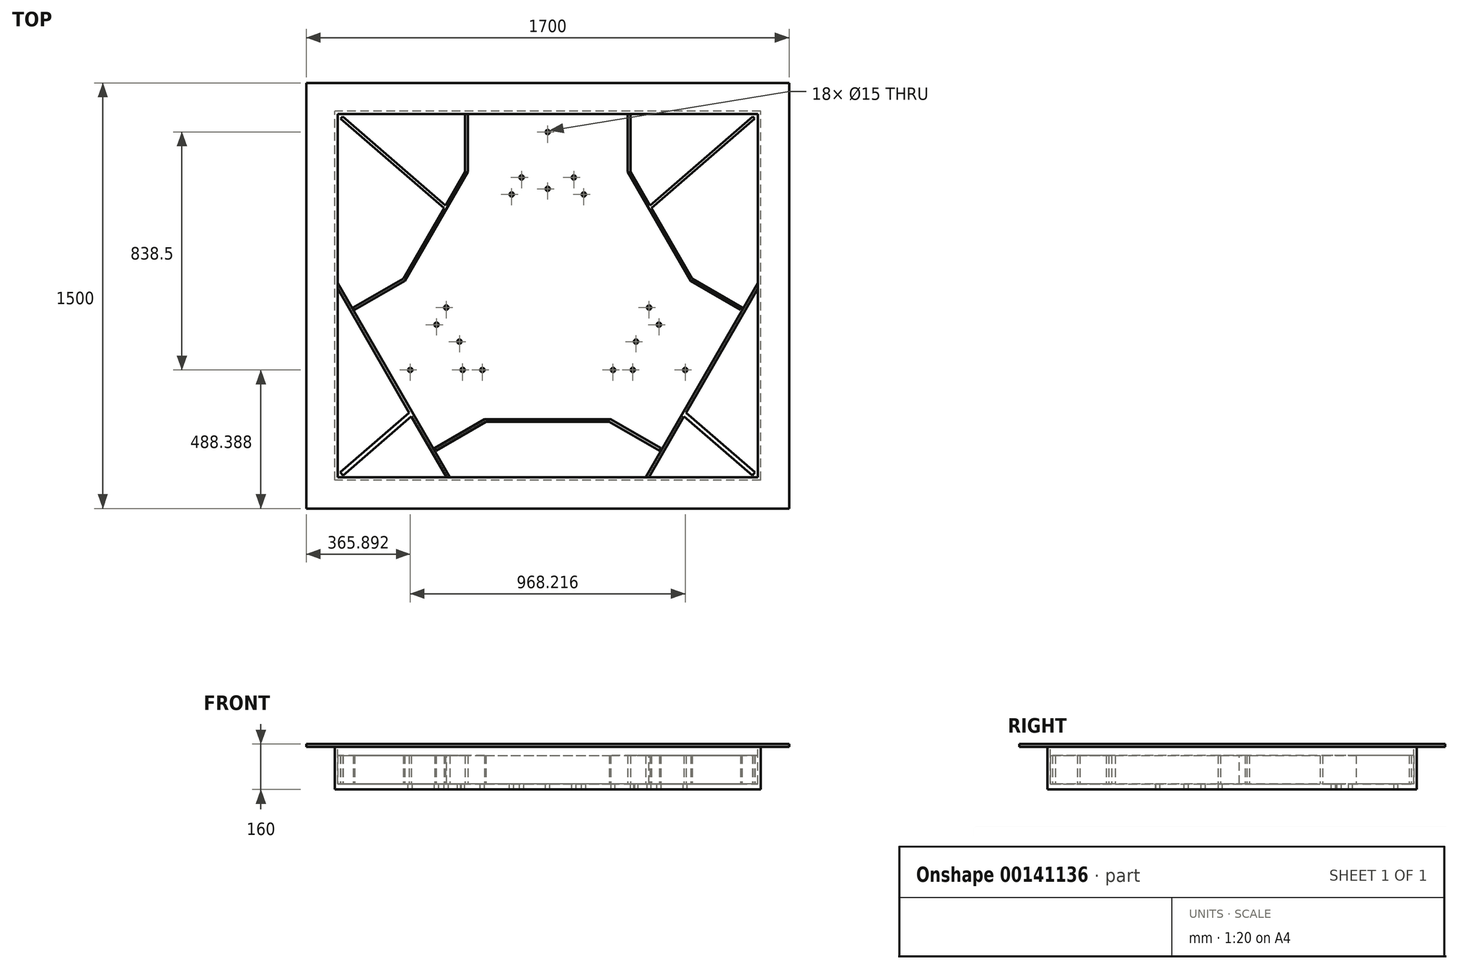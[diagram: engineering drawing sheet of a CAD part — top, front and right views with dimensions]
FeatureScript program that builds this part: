
annotation { "Feature Type Name" : "Feature", "Feature Type Description" : "" }
export const myFeature = defineFeature(function(context is Context, id is Id, definition is map)
    precondition{}
    {
        {
            var Q0;
            Q0=qCreatedBy(makeId("Top.planeOp"),FACE);
            var sketch = newSketch(context, id + "F0", { "sketchPlane" : qUnion([Q0])});
            skLineSegment(sketch, "E0.bottom", {"start": v(750, -650) * mm, "end": v(-750, -650) * mm});
            skLineSegment(sketch, "E0.top", {"start": v(750, 650) * mm, "end": v(-750, 650) * mm});
            skLineSegment(sketch, "E0.left", {"start": v(750, -650) * mm, "end": v(750, 650) * mm});
            skLineSegment(sketch, "E0.right", {"start": v(-750, -650) * mm, "end": v(-750, 650) * mm});
            skPoint(sketch, "E0.middle", {"position": v(0, 0) * mm});
            skSolve(sketch);
        }
        {
            var Q0;
            Q0 = qSketchRegion(id + "F0", true);
            extrude(context, id + "F1", {"entities" : qUnion([Q0]), "depth" : 150 * mm});
        }
        {
            var Q0;
            Q0=makeQuery(id+"F1.opExtrude","CAP_FACE",FACE,{"disambiguationData":[OSD([sQuery(id+"F0.wireOp",EDGE,"E0.bottom"),sQuery(id+"F0.wireOp",EDGE,"E0.top"),sQuery(id+"F0.wireOp",EDGE,"E0.left"),sQuery(id+"F0.wireOp",EDGE,"E0.right")])],"isStart":false});
            var sketch = newSketch(context, id + "F2", { "sketchPlane" : qUnion([Q0])});
            skLineSegment(sketch, "E1", {"start": v(-750, 0) * mm, "end": v(750, 0) * mm, "construction": true});
            skLineSegment(sketch, "E2.bottom", {"start": v(740, -640) * mm, "end": v(-740, -640) * mm});
            skLineSegment(sketch, "E2.top", {"start": v(740, 640) * mm, "end": v(-740, 640) * mm});
            skLineSegment(sketch, "E2.left", {"start": v(740, -640) * mm, "end": v(740, 640) * mm});
            skLineSegment(sketch, "E2.right", {"start": v(-740, -640) * mm, "end": v(-740, 640) * mm});
            skPoint(sketch, "E2.middle", {"position": v(0, 0) * mm});
            skSolve(sketch);
        }
        {
            var Q0;
            Q0 = qSketchRegion(id + "F2", true);
            extrude(context, id + "F3", {"entities" : qUnion([Q0]), "operationType" : NewBodyOperationType.REMOVE, "oppositeDirection" : true, "depth" : 130 * mm});
        }
        {
            var Q0;
            Q0=makeQuery(id+"F1.opExtrude","CAP_FACE",FACE,{"disambiguationData":[OSD([sQuery(id+"F0.wireOp",EDGE,"E0.bottom"),sQuery(id+"F0.wireOp",EDGE,"E0.top"),sQuery(id+"F0.wireOp",EDGE,"E0.left"),sQuery(id+"F0.wireOp",EDGE,"E0.right")])],"isStart":false});
            var sketch = newSketch(context, id + "F4", { "sketchPlane" : qUnion([Q0])});
            skLineSegment(sketch, "E3", {"start": v(0, 650) * mm, "end": v(0, -650) * mm, "construction": true});
            skLineSegment(sketch, "E4.bottom", {"start": v(850, -750) * mm, "end": v(-850, -750) * mm});
            skLineSegment(sketch, "E4.top", {"start": v(850, 750) * mm, "end": v(-850, 750) * mm});
            skLineSegment(sketch, "E4.left", {"start": v(850, -750) * mm, "end": v(850, 750) * mm});
            skLineSegment(sketch, "E4.right", {"start": v(-850, -750) * mm, "end": v(-850, 750) * mm});
            skPoint(sketch, "E4.middle", {"position": v(0, 0) * mm});
            skLineSegment(sketch, "E5.bottom", {"start": v(-740, 640) * mm, "end": v(740, 640) * mm});
            skLineSegment(sketch, "E5.top", {"start": v(-740, -640) * mm, "end": v(740, -640) * mm});
            skLineSegment(sketch, "E5.left", {"start": v(-740, 640) * mm, "end": v(-740, -640) * mm});
            skLineSegment(sketch, "E5.right", {"start": v(740, 640) * mm, "end": v(740, -640) * mm});
            skSolve(sketch);
        }
        {
            var Q0;
            Q0 = qSketchRegion(id + "F4", true);
            extrude(context, id + "F5", {"entities" : qUnion([Q0]), "operationType" : NewBodyOperationType.ADD, "depth" : 10 * mm});
        }
        {
            var Q0;
            Q0=makeQuery(id+"F3.boolean.opBoolean","COPY",FACE,{"derivedFrom":makeQuery(id+"F3.opExtrude","CAP_FACE",FACE,{"disambiguationData":[OSD([sQuery(id+"F2.wireOp",EDGE,"E2.bottom"),sQuery(id+"F2.wireOp",EDGE,"E2.top"),sQuery(id+"F2.wireOp",EDGE,"E2.left"),sQuery(id+"F2.wireOp",EDGE,"E2.right")])],"isStart":false})});
            var sketch = newSketch(context, id + "F6", { "sketchPlane" : qUnion([Q0])});
            skLineSegment(sketch, "E6", {"start": v(0, -640) * mm, "end": v(0, 640) * mm, "construction": true});
            skCircle(sketch, "E7", {"center": v(0, 17.89) * mm, "radius": 559 * mm, "construction": true});
            skCircle(sketch, "E8", {"center": v(0, 576.89) * mm, "radius": 7.5 * mm});
            skLineSegment(sketch, "E9", {"start": v(0, 17.89) * mm, "end": v(-275.24, -141.02) * mm, "construction": true});
            skLineSegment(sketch, "E10", {"start": v(0, 17.89) * mm, "end": v(329.13, -172.14) * mm, "construction": true});
            skCircle(sketch, "E11.MirrorC", {"center": v(-484.1, -261.61) * mm, "radius": 7.5 * mm});
            skCircle(sketch, "E12.MirrorC", {"center": v(484.1, -261.61) * mm, "radius": 7.5 * mm});
            skCircle(sketch, "E13", {"center": v(0, 17.89) * mm, "radius": 362 * mm, "construction": true});
            skCircle(sketch, "E14", {"center": v(0, 17.89) * mm, "radius": 409.5 * mm, "construction": true});
            skCircle(sketch, "E15", {"center": v(-92, 416.92) * mm, "radius": 7.5 * mm});
            skCircle(sketch, "E16.MirrorC", {"center": v(92, 416.92) * mm, "radius": 7.5 * mm});
            skCircle(sketch, "E17", {"center": v(-127, 356.88) * mm, "radius": 7.5 * mm});
            skCircle(sketch, "E18.MirrorC", {"center": v(127, 356.88) * mm, "radius": 7.5 * mm});
            skCircle(sketch, "E19.MirrorC", {"center": v(-230.07, -261.6) * mm, "radius": 7.5 * mm});
            skCircle(sketch, "E20.MirrorC", {"center": v(-357.07, -41.62) * mm, "radius": 7.5 * mm});
            skCircle(sketch, "E21.MirrorC", {"center": v(-299.57, -261.3) * mm, "radius": 7.5 * mm});
            skCircle(sketch, "E22.MirrorC", {"center": v(-391.57, -101.95) * mm, "radius": 7.5 * mm});
            skCircle(sketch, "E23.MirrorC", {"center": v(391.57, -101.95) * mm, "radius": 7.5 * mm});
            skCircle(sketch, "E24.MirrorC", {"center": v(299.57, -261.3) * mm, "radius": 7.5 * mm});
            skCircle(sketch, "E25.MirrorC", {"center": v(230.07, -261.6) * mm, "radius": 7.5 * mm});
            skCircle(sketch, "E26.MirrorC", {"center": v(357.07, -41.62) * mm, "radius": 7.5 * mm});
            skPoint(sketch, "E27.middle", {"position": v(0, 435.08) * mm});
            skCircle(sketch, "E28", {"center": v(0, 376.89) * mm, "radius": 7.5 * mm});
            skCircle(sketch, "E29.MirrorC", {"center": v(310.9, -161.61) * mm, "radius": 7.5 * mm});
            skCircle(sketch, "E30.MirrorC", {"center": v(-310.9, -161.61) * mm, "radius": 7.5 * mm});
            skSolve(sketch);
        }
        {
            var Q0;
            Q0 = qSketchRegion(id + "F6", true);
            extrude(context, id + "F7", {"entities" : qUnion([Q0]), "operationType" : NewBodyOperationType.REMOVE, "endBound" : BoundingType.THROUGH_ALL, "oppositeDirection" : true, "depth" : 25 * mm});
        }
        {
            var Q0;
            Q0=makeQuery(id+"F3.boolean.opBoolean","COPY",FACE,{"derivedFrom":makeQuery(id+"F3.opExtrude","CAP_FACE",FACE,{"disambiguationData":[OSD([sQuery(id+"F2.wireOp",EDGE,"E2.bottom"),sQuery(id+"F2.wireOp",EDGE,"E2.top"),sQuery(id+"F2.wireOp",EDGE,"E2.left"),sQuery(id+"F2.wireOp",EDGE,"E2.right")])],"isStart":false})});
            var sketch = newSketch(context, id + "F8", { "sketchPlane" : qUnion([Q0])});
            skLineSegment(sketch, "E31", {"start": v(-310.9, -161.61) * mm, "end": v(310.9, -161.61) * mm, "construction": true});
            skLineSegment(sketch, "E32", {"start": v(0, 376.89) * mm, "end": v(-310.9, -161.61) * mm, "construction": true});
            skLineSegment(sketch, "E33", {"start": v(0, 376.89) * mm, "end": v(310.9, -161.61) * mm, "construction": true});
            skLineSegment(sketch, "E34", {"start": v(310.9, -161.61) * mm, "end": v(-155.45, 107.64) * mm, "construction": true});
            skLineSegment(sketch, "E35", {"start": v(0, 376.89) * mm, "end": v(0, -161.61) * mm, "construction": true});
            skLineSegment(sketch, "E36", {"start": v(-310.9, -161.61) * mm, "end": v(155.45, 107.64) * mm, "construction": true});
            skLineSegment(sketch, "E37.bottom", {"start": v(210, 596.89) * mm, "end": v(-210, 596.89) * mm, "construction": true});
            skLineSegment(sketch, "E37.top", {"start": v(210, 296.89) * mm, "end": v(-210, 296.89) * mm, "construction": true});
            skLineSegment(sketch, "E37.left", {"start": v(210, 596.89) * mm, "end": v(210, 296.89) * mm, "construction": true});
            skLineSegment(sketch, "E37.right", {"start": v(-210, 596.89) * mm, "end": v(-210, 296.89) * mm, "construction": true});
            skPoint(sketch, "E37.middle", {"position": v(0, 446.89) * mm});
            skLineSegment(sketch, "E38.MirrorCS", {"start": v(396.43, -453.48) * mm, "end": v(136.62, -303.48) * mm, "construction": true});
            skLineSegment(sketch, "E39.MirrorCS", {"start": v(606.43, -89.75) * mm, "end": v(396.43, -453.48) * mm, "construction": true});
            skLineSegment(sketch, "E40.MirrorCS", {"start": v(606.43, -89.75) * mm, "end": v(346.62, 60.25) * mm, "construction": true});
            skLineSegment(sketch, "E41.MirrorCS", {"start": v(346.62, 60.25) * mm, "end": v(136.62, -303.48) * mm, "construction": true});
            skLineSegment(sketch, "E42", {"start": v(0, 576.89) * mm, "end": v(58.05, 576.89) * mm, "construction": true});
            skLineSegment(sketch, "E43.MirrorCS", {"start": v(-136.62, -303.48) * mm, "end": v(-346.62, 60.25) * mm, "construction": true});
            skLineSegment(sketch, "E44.MirrorCS", {"start": v(-606.43, -89.75) * mm, "end": v(-346.62, 60.25) * mm, "construction": true});
            skLineSegment(sketch, "E45.MirrorCS", {"start": v(-396.43, -453.48) * mm, "end": v(-606.43, -89.75) * mm, "construction": true});
            skLineSegment(sketch, "E46.MirrorCS", {"start": v(-396.43, -453.48) * mm, "end": v(-136.62, -303.48) * mm, "construction": true});
            skLineSegment(sketch, "E47", {"start": v(-281.26, 436.89) * mm, "end": v(-281.26, 640) * mm});
            skLineSegment(sketch, "E48", {"start": v(-281.26, 640) * mm, "end": v(-291.26, 640) * mm});
            skLineSegment(sketch, "E49", {"start": v(-291.26, 640) * mm, "end": v(-291.26, 436.89) * mm});
            skLineSegment(sketch, "E50", {"start": v(-291.26, 436.89) * mm, "end": v(-281.26, 436.89) * mm});
            skLineSegment(sketch, "E51.MirrorCS", {"start": v(291.26, 640) * mm, "end": v(291.26, 436.89) * mm});
            skLineSegment(sketch, "E52.MirrorCS", {"start": v(281.26, 436.89) * mm, "end": v(281.26, 640) * mm});
            skLineSegment(sketch, "E53.MirrorCS", {"start": v(291.26, 436.89) * mm, "end": v(281.26, 436.89) * mm});
            skLineSegment(sketch, "E54.MirrorCS", {"start": v(281.26, 640) * mm, "end": v(291.26, 640) * mm});
            skLineSegment(sketch, "E55", {"start": v(-740, 640) * mm, "end": v(740, -640) * mm, "construction": true});
            skLineSegment(sketch, "E56.MirrorCS", {"start": v(393.14, -545.4) * mm, "end": v(217.24, -443.85) * mm});
            skLineSegment(sketch, "E57.MirrorCS", {"start": v(222.24, -435.19) * mm, "end": v(398.14, -536.75) * mm});
            skLineSegment(sketch, "E58.MirrorCS", {"start": v(398.14, -536.75) * mm, "end": v(393.14, -545.4) * mm});
            skLineSegment(sketch, "E59", {"start": v(-728.87, 623.77) * mm, "end": v(-725.6, 627.55) * mm});
            skLineSegment(sketch, "E60.MirrorCS", {"start": v(-722.33, 631.33) * mm, "end": v(-359.95, 317.92) * mm});
            skLineSegment(sketch, "E61", {"start": v(740, 640) * mm, "end": v(-740, -640) * mm, "construction": true});
            skLineSegment(sketch, "E62.MirrorCS", {"start": v(-503.5, 51.96) * mm, "end": v(-679.4, -49.6) * mm});
            skLineSegment(sketch, "E63.MirrorCS", {"start": v(-684.4, -40.93) * mm, "end": v(-508.5, 60.63) * mm});
            skLineSegment(sketch, "E64.MirrorCS", {"start": v(-679.4, -49.6) * mm, "end": v(-684.4, -40.93) * mm});
            skLineSegment(sketch, "E65.MirrorCS", {"start": v(503.5, 51.96) * mm, "end": v(679.4, -49.6) * mm});
            skLineSegment(sketch, "E66.MirrorCS", {"start": v(684.4, -40.93) * mm, "end": v(508.5, 60.63) * mm});
            skLineSegment(sketch, "E67.MirrorCS", {"start": v(508.5, 60.63) * mm, "end": v(503.5, 51.96) * mm});
            skLineSegment(sketch, "E68.MirrorCS", {"start": v(679.4, -49.6) * mm, "end": v(684.4, -40.93) * mm});
            skLineSegment(sketch, "E69", {"start": v(-281.26, 436.89) * mm, "end": v(-503.5, 51.96) * mm});
            skLineSegment(sketch, "E70", {"start": v(-508.5, 60.63) * mm, "end": v(-291.26, 436.89) * mm});
            skLineSegment(sketch, "E71.MirrorCS", {"start": v(-222.24, -435.19) * mm, "end": v(-398.14, -536.75) * mm});
            skLineSegment(sketch, "E72.MirrorCS", {"start": v(-393.14, -545.4) * mm, "end": v(-217.24, -443.85) * mm});
            skLineSegment(sketch, "E73.MirrorCS", {"start": v(-398.14, -536.75) * mm, "end": v(-393.14, -545.4) * mm});
            skLineSegment(sketch, "E74", {"start": v(-740, 44.84) * mm, "end": v(-344.6, -640) * mm});
            skLineSegment(sketch, "E75", {"start": v(-344.6, -640) * mm, "end": v(-353.1, -644.9) * mm});
            skLineSegment(sketch, "E76", {"start": v(-353.1, -644.9) * mm, "end": v(-748.5, 39.94) * mm});
            skLineSegment(sketch, "E77", {"start": v(-748.5, 39.94) * mm, "end": v(-740, 44.84) * mm});
            skLineSegment(sketch, "E78.MirrorCS", {"start": v(740, 44.84) * mm, "end": v(344.6, -640) * mm});
            skLineSegment(sketch, "E79.MirrorCS", {"start": v(353.1, -644.9) * mm, "end": v(748.5, 39.94) * mm});
            skLineSegment(sketch, "E80.MirrorCS", {"start": v(748.5, 39.94) * mm, "end": v(740, 44.84) * mm});
            skLineSegment(sketch, "E81.MirrorCS", {"start": v(344.6, -640) * mm, "end": v(353.1, -644.9) * mm});
            skLineSegment(sketch, "E82.MirrorCS", {"start": v(281.26, 436.89) * mm, "end": v(503.5, 51.96) * mm});
            skLineSegment(sketch, "E83.MirrorCS", {"start": v(508.5, 60.63) * mm, "end": v(291.26, 436.89) * mm});
            skLineSegment(sketch, "E84.MirrorCS", {"start": v(503.5, 51.96) * mm, "end": v(508.5, 60.63) * mm});
            skPoint(sketch, "E85.cornerSnap0", {"position": v(77.73, -26.99) * mm});
            skLineSegment(sketch, "E86", {"start": v(0, -435.19) * mm, "end": v(-222.24, -435.19) * mm});
            skLineSegment(sketch, "E87", {"start": v(-217.24, -443.85) * mm, "end": v(0, -443.85) * mm});
            skLineSegment(sketch, "E88.MirrorCS", {"start": v(0, -435.19) * mm, "end": v(222.24, -435.19) * mm});
            skLineSegment(sketch, "E89.MirrorCS", {"start": v(217.24, -443.85) * mm, "end": v(0, -443.85) * mm});
            skLineSegment(sketch, "E90.MirrorCS", {"start": v(-722.33, 631.33) * mm, "end": v(-725.6, 627.55) * mm});
            skLineSegment(sketch, "E91", {"start": v(-728.87, 623.77) * mm, "end": v(-365.04, 309.1) * mm});
            skLineSegment(sketch, "E92.MirrorCS", {"start": v(722.33, 631.33) * mm, "end": v(359.95, 317.92) * mm});
            skLineSegment(sketch, "E93.MirrorCS", {"start": v(728.87, 623.77) * mm, "end": v(365.04, 309.1) * mm});
            skLineSegment(sketch, "E94.MirrorCS", {"start": v(728.87, 623.77) * mm, "end": v(725.6, 627.55) * mm});
            skLineSegment(sketch, "E95.MirrorCS", {"start": v(722.33, 631.33) * mm, "end": v(725.6, 627.55) * mm});
            skLineSegment(sketch, "E96", {"start": v(-487.54, -412.06) * mm, "end": v(-730.43, -622.13) * mm});
            skLineSegment(sketch, "E97", {"start": v(-730.43, -622.13) * mm, "end": v(-725.68, -627.62) * mm});
            skLineSegment(sketch, "E98.MirrorCS", {"start": v(-720.94, -633.1) * mm, "end": v(-725.68, -627.62) * mm});
            skLineSegment(sketch, "E99", {"start": v(-720.94, -633.1) * mm, "end": v(-480.15, -424.86) * mm});
            skLineSegment(sketch, "E100.MirrorCS", {"start": v(720.94, -633.1) * mm, "end": v(480.15, -424.86) * mm});
            skLineSegment(sketch, "E101.MirrorCS", {"start": v(487.54, -412.06) * mm, "end": v(730.43, -622.13) * mm});
            skLineSegment(sketch, "E102.MirrorCS", {"start": v(730.43, -622.13) * mm, "end": v(725.68, -627.62) * mm});
            skLineSegment(sketch, "E103.MirrorCS", {"start": v(720.94, -633.1) * mm, "end": v(725.68, -627.62) * mm});
            skSolve(sketch);
        }
        {
            var Q0;
            Q0 = qSketchRegion(id + "F8", true);
            extrude(context, id + "F9", {"entities" : qUnion([Q0]), "operationType" : NewBodyOperationType.ADD, "depth" : 100 * mm});
        }
    });
